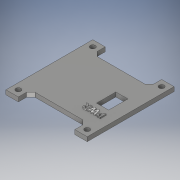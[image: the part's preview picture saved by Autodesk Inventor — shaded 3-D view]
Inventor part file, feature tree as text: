
AUTODESK INVENTOR PART (.ipt)
format: ipt  version: 2018 (Build 220112000, 112)  size: 587,776 bytes
history: native  units: in
note: dims shown in document units (in); Inventor stores cm internally (conversion verified against a paired STEP export)
features: sketch x4, extrude x3, move_body x3, direct_edit x2, emboss x1, chamfer x1
ambient origin geometry x8: Origin, YZ Plane, XZ Plane, XY Plane, X Axis, Y Axis, Z Axis, Center Point
bodies: Solid1 (feature_tree)
feature tree (14):
  extrude  "Extrusion1"  Depth=0.36in
  extrude  "Extrusion2"  Depth=0.36in
  extrude  "Extrusion3"  Depth=0.36in
  emboss  "Emboss1"
  chamfer  "Chamfer1"  Distance=0.125in
  direct_edit  "Direct Edit1"
  direct_edit  "Direct Edit2"
  sketch  "Sketch1"  dims[d0=2.311in d1=0.36in]
  sketch  "Sketch2"  dims[d2=0.36in d3=0.36in]
  sketch  "Sketch3"  dims[d4=0.36in d5=0.36in]
  sketch  "Sketch5"  dims[d7=0.36in d8=0.125in d9=0.0in d10=0.146in d11=0.146in d12=0.146in d13=0.146in d14=1.0in d15=0.0in d16=3.9in d17=0.18in d18=0.181in d19=0.18in d20=0.18in d21=0.181in d22=0.18in d23=0.18in d24=0.18in d25=0.56in d26=0.35in d27=0.35in d28=0.25in d30=1.0in d31=0.0in d32=0.36in d37=0.035in d38=0.0in d64=0.125in d65=0.125in d66=45.0deg d67=0.0in d68=0.0in d69=0.105in d70=0.0in d71=0.0in d72=0.105in d73=0.0in d74=0.0in d75=-1.54in]
  move_body  "Move1"
  move_body  "Move2"
  move_body  "Move3"
